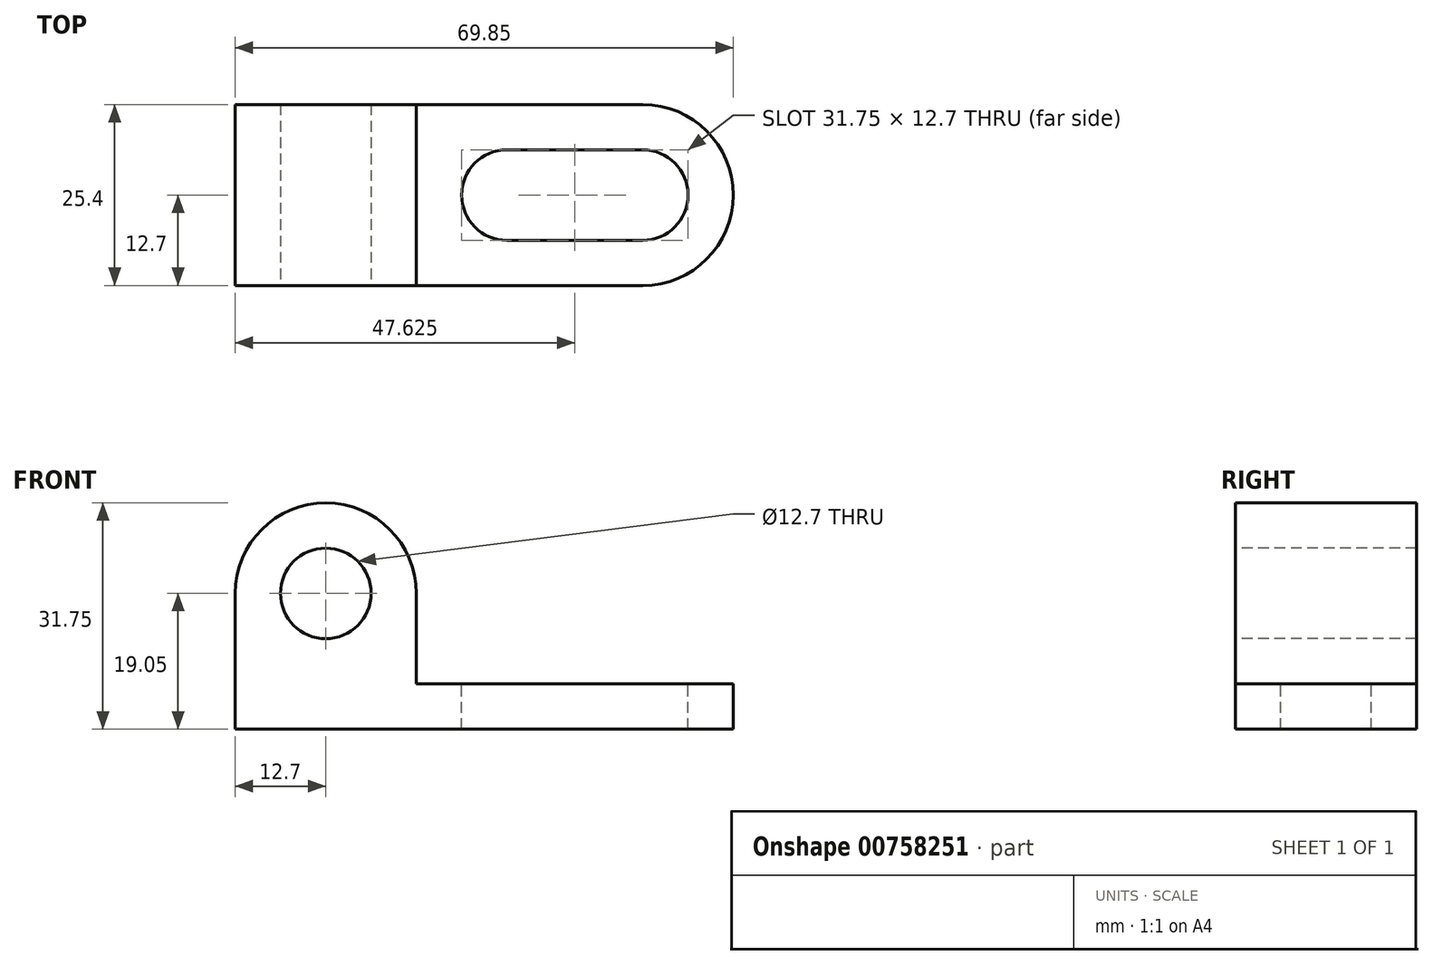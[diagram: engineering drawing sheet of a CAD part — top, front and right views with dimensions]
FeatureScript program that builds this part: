
annotation { "Feature Type Name" : "Feature", "Feature Type Description" : "" }
export const myFeature = defineFeature(function(context is Context, id is Id, definition is map)
    precondition{}
    {
        {
            var Q0;
            Q0=qCreatedBy(makeId("Front.planeOp"),FACE);
            var sketch = newSketch(context, id + "F0", { "sketchPlane" : qUnion([Q0])});
            skLineSegment(sketch, "E0", {"start": v(0, 0) * mm, "end": v(0, 31.75) * mm});
            skLineSegment(sketch, "E1", {"start": v(0, 31.75) * mm, "end": v(25.4, 31.75) * mm});
            skLineSegment(sketch, "E2", {"start": v(25.4, 31.75) * mm, "end": v(25.4, 6.35) * mm});
            skLineSegment(sketch, "E3", {"start": v(25.4, 6.35) * mm, "end": v(69.85, 6.35) * mm});
            skLineSegment(sketch, "E4", {"start": v(69.85, 6.35) * mm, "end": v(69.85, 0) * mm});
            skLineSegment(sketch, "E5", {"start": v(69.85, 0) * mm, "end": v(0, 0) * mm});
            skSolve(sketch);
        }
        {
            var Q0;
            Q0=makeQuery(id+"F0.imprint","IMPRINT",FACE,{"disambiguationData":[TD([[makeQuery(id+"F0.imprint","IMPRINT",EDGE,{"derivedFrom":sQuery(id+"F0.wireOp",EDGE,"E0")}),-1.0]])]});
            extrude(context, id + "F1", {"entities" : qUnion([Q0]), "depth" : 25.4 * mm, "offsetDistance" : 25.4 * mm});
        }
        {
            var Q0;
            Q0=makeQuery(id+"F1.opExtrude","CAP_FACE",FACE,{"disambiguationData":[OSD([sQuery(id+"F0.wireOp",EDGE,"E0"),sQuery(id+"F0.wireOp",EDGE,"E1"),sQuery(id+"F0.wireOp",EDGE,"E2"),sQuery(id+"F0.wireOp",EDGE,"E3"),sQuery(id+"F0.wireOp",EDGE,"E4"),sQuery(id+"F0.wireOp",EDGE,"E5")])],"isStart":false});
            var sketch = newSketch(context, id + "F2", { "sketchPlane" : qUnion([Q0])});
            skCircle(sketch, "E6", {"center": v(12.7, 19.05) * mm, "radius": 6.35 * mm});
            skArc(sketch, "E7", {"start": v(25.4, 19.05) * mm, "mid": v(12.7, 31.75) * mm, "end": v(0, 19.05) * mm});
            skSolve(sketch);
        }
        {
            var Q0;
            {var subQ0=sQuery(id+"F2.wireOp",EDGE,"E7");var subQ1=makeQuery(id+"F1.opExtrude","CAP_EDGE",EDGE,{"disambiguationData":[OSD([sQuery(id+"F0.wireOp",EDGE,"E0")])],"isStart":false});var subQ2=makeQuery(id+"F2.imprint","INTERSECT",VERTEX,{"derivedFrom":[subQ1,subQ0]});Q0=makeQuery(id+"F2.imprint","IMPRINT",FACE,{"disambiguationData":[TD([[makeQuery(id+"F2.imprint","IMPRINT",EDGE,{"disambiguationData":[TD([[subQ2,1.0]])],"derivedFrom":subQ0}),-1.0]])]});}
            var Q1;
            {var subQ0=sQuery(id+"F2.wireOp",EDGE,"E7");var subQ1=makeQuery(id+"F1.opExtrude","CAP_EDGE",EDGE,{"disambiguationData":[OSD([sQuery(id+"F0.wireOp",EDGE,"E2")])],"isStart":false});var subQ2=makeQuery(id+"F2.imprint","INTERSECT",VERTEX,{"derivedFrom":[subQ1,subQ0]});Q1=makeQuery(id+"F2.imprint","IMPRINT",FACE,{"disambiguationData":[TD([[makeQuery(id+"F2.imprint","IMPRINT",EDGE,{"disambiguationData":[TD([[subQ2,-1.0]])],"derivedFrom":subQ0}),-1.0]])]});}
            var Q2;
            Q2=makeQuery(id+"F2.imprint","IMPRINT",FACE,{"disambiguationData":[TD([[makeQuery(id+"F2.imprint","IMPRINT",EDGE,{"derivedFrom":sQuery(id+"F2.wireOp",EDGE,"E6")}),1.0]])]});
            extrude(context, id + "F3", {"entities" : qUnion([Q0, Q1, Q2]), "operationType" : NewBodyOperationType.REMOVE, "oppositeDirection" : true, "depth" : 25.4 * mm, "offsetDistance" : 25.4 * mm});
        }
        {
            var Q0;
            Q0=makeQuery(id+"F1.opExtrude","SWEPT_FACE",FACE,{"disambiguationData":[OSD([sQuery(id+"F0.wireOp",EDGE,"E3")])]});
            var sketch = newSketch(context, id + "F4", { "sketchPlane" : qUnion([Q0])});
            skCircle(sketch, "E8", {"center": v(57.15, -12.7) * mm, "radius": 6.35 * mm});
            skCircle(sketch, "E9", {"center": v(38.1, -12.7) * mm, "radius": 6.35 * mm});
            skLineSegment(sketch, "E10", {"start": v(38.1, -12.7) * mm, "end": v(38.1, -19.05) * mm});
            skLineSegment(sketch, "E11", {"start": v(38.1, -19.05) * mm, "end": v(57.15, -19.05) * mm});
            skLineSegment(sketch, "E12", {"start": v(57.15, -19.05) * mm, "end": v(57.15, -6.35) * mm});
            skLineSegment(sketch, "E13", {"start": v(57.15, -6.35) * mm, "end": v(38.1, -6.35) * mm});
            skLineSegment(sketch, "E14", {"start": v(38.1, -6.35) * mm, "end": v(38.1, -12.7) * mm});
            skArc(sketch, "E15", {"start": v(57.15, -25.4) * mm, "mid": v(69.85, -12.7) * mm, "end": v(57.15, 0) * mm});
            skSolve(sketch);
        }
        {
            var Q0;
            {var subQ0=sQuery(id+"F4.wireOp",EDGE,"E10");Q0=makeQuery(id+"F4.imprint","IMPRINT",FACE,{"disambiguationData":[TD([[makeQuery(id+"F4.imprint","IMPRINT",EDGE,{"derivedFrom":subQ0}),-1.0]])]});}
            var Q1;
            {var subQ0=sQuery(id+"F4.wireOp",EDGE,"E10");Q1=makeQuery(id+"F4.imprint","IMPRINT",FACE,{"disambiguationData":[TD([[makeQuery(id+"F4.imprint","IMPRINT",EDGE,{"derivedFrom":subQ0}),1.0]])]});}
            var Q2;
            {var subQ1=sQuery(id+"F4.wireOp",EDGE,"E11");Q2=makeQuery(id+"F4.imprint","IMPRINT",FACE,{"disambiguationData":[TD([[makeQuery(id+"F4.imprint","IMPRINT",EDGE,{"derivedFrom":subQ1}),1.0]])]});}
            var Q3;
            {var subQ0=sQuery(id+"F4.wireOp",EDGE,"E15");var subQ1=sQuery(id+"F0.wireOp",EDGE,"E3");var subQ2=makeQuery(id+"F1.opExtrude","CAP_EDGE",EDGE,{"disambiguationData":[OSD([subQ1])],"isStart":true});var subQ3=makeQuery(id+"F4.imprint","INTERSECT",VERTEX,{"derivedFrom":[subQ2,subQ0]});Q3=makeQuery(id+"F4.imprint","IMPRINT",FACE,{"disambiguationData":[TD([[makeQuery(id+"F4.imprint","IMPRINT",EDGE,{"disambiguationData":[TD([[subQ3,1.0]])],"derivedFrom":subQ0}),-1.0]])]});}
            var Q4;
            {var subQ0=sQuery(id+"F4.wireOp",EDGE,"E15");var subQ1=sQuery(id+"F0.wireOp",EDGE,"E3");var subQ2=makeQuery(id+"F1.opExtrude","CAP_EDGE",EDGE,{"disambiguationData":[OSD([subQ1])],"isStart":false});var subQ3=makeQuery(id+"F4.imprint","INTERSECT",VERTEX,{"derivedFrom":[subQ2,subQ0]});Q4=makeQuery(id+"F4.imprint","IMPRINT",FACE,{"disambiguationData":[TD([[makeQuery(id+"F4.imprint","IMPRINT",EDGE,{"disambiguationData":[TD([[subQ3,-1.0]])],"derivedFrom":subQ0}),-1.0]])]});}
            var Q5;
            {var subQ0=sQuery(id+"F4.wireOp",EDGE,"E12");Q5=makeQuery(id+"F4.imprint","IMPRINT",FACE,{"disambiguationData":[TD([[makeQuery(id+"F4.imprint","IMPRINT",EDGE,{"derivedFrom":subQ0}),-1.0]])]});}
            var Q6;
            {var subQ0=sQuery(id+"F4.wireOp",EDGE,"E12");Q6=makeQuery(id+"F4.imprint","IMPRINT",FACE,{"disambiguationData":[TD([[makeQuery(id+"F4.imprint","IMPRINT",EDGE,{"derivedFrom":subQ0}),1.0]])]});}
            extrude(context, id + "F5", {"entities" : qUnion([Q0, Q1, Q2, Q3, Q4, Q5, Q6]), "operationType" : NewBodyOperationType.REMOVE, "oppositeDirection" : true, "depth" : 12.7 * mm, "offsetDistance" : 25.4 * mm});
        }
    });
